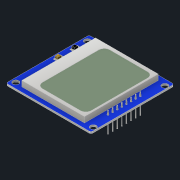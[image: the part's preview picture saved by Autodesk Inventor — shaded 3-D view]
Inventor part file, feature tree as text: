
AUTODESK INVENTOR PART (.ipt)
format: ipt  version: 2022 (Build 260153000, 153)  size: 319,488 bytes
history: native  units: in
note: dims shown in document units (in); Inventor stores cm internally (conversion verified against a paired STEP export)
features: extrude x9, sketch x9, draft x8, pattern_linear x3, fillet x3, projected_geometry x1
ambient origin geometry x8: Origin, YZ Plane, XZ Plane, XY Plane, X Axis, Y Axis, Z Axis, Center Point
bodies: Solid1 (feature_tree)
feature tree (33):
  extrude  "Extrusion1"  Depth=1.7717in
  extrude  "Extrusion2"  Depth=1.3386in
  extrude  "Extrusion3"  Depth=0.1181in TaperAngle=0.0deg
  extrude  "Extrusion4"  Depth=0.2362in
  extrude  "Extrusion5"  Depth=1.437in
  pattern_linear  "Rectangular Pattern1"  Spacing1=0.126in  [1 undecoded]
  fillet  "Fillet1"  Radius=0.0906in
  fillet  "Fillet2"  Radius=0.1181in
  extrude  "Extrusion6"  Depth=0.0984in
  extrude  "Extrusion7"  Depth=0.0984in TaperAngle=0.0deg
  fillet  "Fillet3"  Radius=0.0197in
  extrude  "Extrusion8"  Depth=0.1378in
  pattern_linear  "Rectangular Pattern2"  Spacing1=0.502in  [1 undecoded]
  extrude  "Extrusion9"  Depth=0.0984in TaperAngle=0.0deg
  pattern_linear  "Rectangular Pattern3"  Count1=8 Spacing1=0.0984in
  draft  "FaceDraft1"
  draft  "FaceDraft2"
  draft  "FaceDraft3"
  draft  "FaceDraft4"
  draft  "FaceDraft5"
  draft  "FaceDraft6"
  draft  "FaceDraft7"
  draft  "FaceDraft8"
  sketch  "Sketch1"  dims[d0=1.811in d1=1.7717in]
  sketch  "Sketch2"  dims[d2=0.0394in d3=0.0in d4=1.3386in]
  sketch  "Sketch3"  dims[d5=1.5748in d6=0.1181in d7=0.0in]
  sketch  "Sketch4"  dims[d8=0.2362in d9=0.2362in]
  sketch  "Sketch5"  dims[d10=1.0433in d11=1.437in]
  sketch  "Sketch7"  dims[d13=0.0394in]
  sketch  "Sketch8"  dims[d14=0.002in d15=0.0in]
  sketch  "Sketch9"  dims[d16=0.126in]
  projected_geometry  "Projected Loop2"
  sketch  "Sketch10"  dims[d19=0.126in d22=0.126in d23=0.0906in d24=0.1181in d25=0.126in d28=0.0039in d29=0.0in d32=0.0197in d33=0.1378in d34=0.502in d35=0.0039in d36=0.0in d37=3.1496in d39=0.0984in d43=0.0394in d44=0.1181in d45=0.0591in d46=0.1575in d47=0.002in d48=0.0in d49=0.1181in d50=0.8268in d51=0.0591in d52=0.4724in d53=0.0787in d54=0.0394in d55=0.0394in d56=0.0787in d57=0.0394in d58=0.0394in d59=0.0in d60=0.0098in d61=0.0984in d63=0.0787in d64=0.0in d65=3.1496in d67=0.0984in d68=0.0197in d69=0.2362in d70=0.0in d71=0.1969in d72=0.0in d73=3.1496in d75=0.0984in d76=0.0344in d77=0.0344in d78=0.0344in d79=0.0344in d80=0.0344in d81=0.0344in d82=0.0344in d83=0.0344in d84=1.5276in d85=1.6535in]
note: 2 required parameter values undecoded (feature->parameter linkage not recoverable at this tier; creation-order binding heuristic only, values carry confidence <= 0.55)
